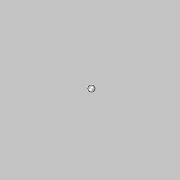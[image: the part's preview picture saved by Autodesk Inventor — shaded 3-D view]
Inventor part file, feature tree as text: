
AUTODESK INVENTOR PART (.ipt)
format: ipt  version: 2017 (Build 210142000, 142)  size: 133,632 bytes
history: native  units: mm
features: sketch x10, extrude x9, hole x2, mirror x1
ambient origin geometry x8: Origin, YZ Plane, XZ Plane, XY Plane, X Axis, Y Axis, Z Axis, Center Point
bodies: Solid1 (feature_tree)
feature tree (22):
  extrude  "Extrusion1"  Depth=85.0mm
  hole  "Hole1"  [1 undecoded]
  hole  "Hole2"  [1 undecoded]
  extrude  "Extrusion2"  Depth=12.0mm TaperAngle=0.0deg
  sketch  "Sketch5"  dims[d15=36.752mm d16=80.0mm d17=10.0mm d18=5.5mm d19=90.0deg d20=25.0mm d21=0.0mm d22=12.0mm d23=0.0mm]
  extrude  "Extrusion3"  Depth=25.0mm
  extrude  "Extrusion4"  Depth=15.0mm
  extrude  "Extrusion5"  Depth=10.0mm
  mirror  "Mirror1"
  extrude  "Extrusion6"  Depth=30.0mm TaperAngle=0.0deg
  extrude  "Extrusion7"  Depth=32.0mm
  extrude  "Extrusion8"  Depth=21.0mm
  extrude  "Extrusion9"  Depth=38.0mm
  sketch  "Sketch1"  dims[d0=85.0mm d1=85.0mm]
  sketch  "Sketch2"  dims[d2=135.0mm d3=0.0mm d4=70.0mm]
  sketch  "Sketch3"  dims[d5=70.0mm d6=7.5mm]
  sketch  "Sketch4"  dims[d7=5.5mm d8=10.0mm d9=10.0mm d10=5.5mm d11=90.0deg d12=14.2mm d13=20.594885mm]
  sketch  "Sketch7"  dims[d24=15.0mm d25=25.0mm]
  sketch  "Sketch8"  dims[d26=7.0mm d27=0.0mm d28=15.0mm]
  sketch  "Sketch9"  dims[d29=25.0mm d30=0.0mm d31=10.0mm]
  sketch  "Sketch10"  dims[d32=1.5mm d33=30.0mm d34=0.0mm]
  sketch  "Sketch11"  dims[d35=30.0mm d37=32.0mm d38=21.0mm d39=38.0mm d40=42.0mm d41=22.0mm d42=24.0mm d43=15.0mm d44=0.0mm d45=12.0mm d46=50.0mm d47=0.0mm d48=60.0mm d49=10.0mm d50=0.0mm d51=45.0mm d52=30.0mm d53=0.0mm d54=0.0mm]
note: 2 required parameter values undecoded (feature->parameter linkage not recoverable at this tier; creation-order binding heuristic only, values carry confidence <= 0.55)
